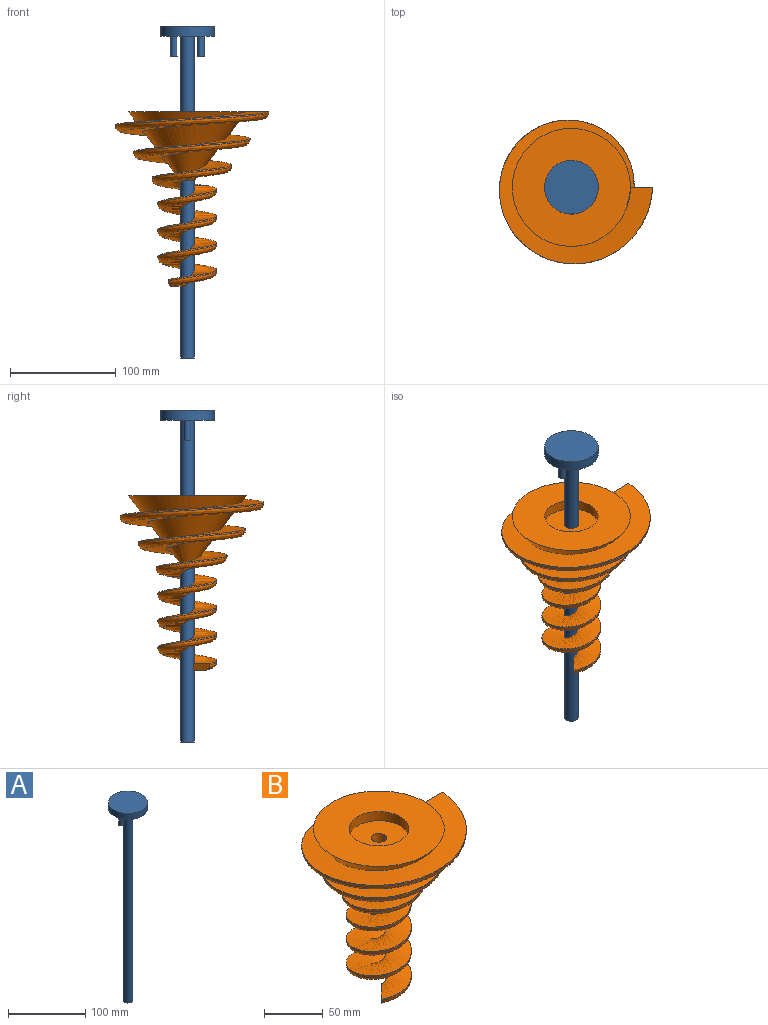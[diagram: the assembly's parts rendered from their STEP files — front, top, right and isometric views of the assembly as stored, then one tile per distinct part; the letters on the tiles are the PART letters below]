
ASSEMBLY  parts=2 mates=1
PART A: 9 faces, bbox 50.8x50.8x314.3 mm
  f0: cylinder r=25.4mm len=50.8mm, axis (0,0,1), area 1520.1mm2, adj f1,f2
  f1: plane 50.8x50.8mm, normal (0,0,-1), area 1836.8mm2, adj f0,f3,f5,f7
  f2: plane 50.8x50.8mm, normal (0,0,1), area 2026.8mm2, adj f0
  f3: cylinder r=6.35mm len=304.8mm, axis (0,0,1), area 12161mm2, adj f1,f4
  f4: plane 12.7x12.7mm, normal (0,0,-1), area 126.7mm2, adj f3
  f5: cylinder r=3.17mm len=19.05mm, axis (0,0,1), area 380mm2, adj f1,f6
  f6: plane 6.35x6.35mm, normal (0,0,-1), area 31.7mm2, adj f5
  f7: cylinder r=3.17mm len=19.05mm, axis (0,0,1), area 380mm2, adj f1,f8
  f8: plane 6.35x6.35mm, normal (0,0,-1), area 31.7mm2, adj f7
PART B: 36 faces, bbox 145.4x137.7x165.3 mm
  f0: bspline ~89.48x85.12mm, area 645.8mm2, adj f1,f5,f9,f21,f22,f23
  f1: cone r=55.88mm half-angle=37.4deg, axis (0,0,1), area 12469.1mm2, adj f0,f2,f4,f5,f6,f9,f17,f18
  f2: plane 25.8x6.35mm, normal (0,1,0), area 142.9mm2, adj f1,f3,f4,f5,f31
  f3: bspline ~145.32x137.61mm, area 1159.1mm2, adj f2,f4,f29,f31
  f4: bspline ~145.32x137.61mm, area 16660.8mm2, adj f1,f2,f3,f9,f17,f18,f20,f30
  f5: bspline ~145.32x137.61mm, area 13749.4mm2, adj f0,f1,f2,f9,f24,f25,f26,f28
  f6: plane 111.76x111.76mm, normal (0,0,1), area 7783mm2, adj f1,f7
  f7: cylinder r=25.4mm len=50.8mm, axis (0,0,1), area 1520.1mm2, adj f6,f8
  f8: plane 50.8x50.8mm, normal (0,0,1), area 1895mm2, adj f7,f9
  f9: cylinder r=6.48mm len=71.01mm, axis (0,0,1), area 2363.8mm2, adj f0,f1,f4,f5,f8,f10,f14,f15
  f10: cylinder r=6.48mm len=31.75mm, axis (0,0,1), area 258.4mm2, adj f9,f11,f28,f30
  f11: cylinder r=6.48mm len=31.75mm, axis (0,0,1), area 258.4mm2, adj f10,f12,f28,f30
  f12: cylinder r=6.48mm len=31.75mm, axis (0,0,1), area 258.4mm2, adj f11,f13,f28,f30
  f13: cylinder r=6.48mm len=14.71mm, axis (0,0,1), area 85.1mm2, adj f12,f27,f28,f30
  f14: bspline ~4.57x2.65mm, area 0mm2, adj f9,f15,f16
  f15: bspline ~7.2x7.06mm, area 3.7mm2, adj f9,f14,f16
  f16: plane 3.92x2.43mm, normal (0.39,0.74,-0.55), area 0.5mm2, adj f9,f14,f15
  f17: bspline ~2.12x1.49mm, area 0.6mm2, adj f1,f4,f19,f20
  f18: bspline ~4.45x2.8mm, area 1.8mm2, adj f1,f4,f19,f20
  f19: bspline ~2.48x1.6mm, area 1.4mm2, adj f1,f17,f18,f20
  f20: plane 0.69x0.46mm, normal (0.39,0.74,-0.55), area 0.2mm2, adj f4,f17,f18,f19
  f21: bspline ~76.8x75.65mm, area 538.5mm2, adj f0,f1,f22
  f22: bspline ~84.06x75.39mm, area 149.2mm2, adj f0,f1,f21,f23
  f23: bspline ~76.08x74.82mm, area 439.7mm2, adj f0,f1,f22
  f24: bspline ~2.34x1.4mm, area 0.7mm2, adj f5,f25,f26
  f25: plane 2.3x1.23mm, normal (0.39,0.74,-0.55), area 0.2mm2, adj f5,f24,f26
  f26: bspline ~7.7x4.39mm, area 0.1mm2, adj f5,f24,f25
  f27: plane 15.4x15.17mm, normal (-0.71,0.7,0), area 131.8mm2, adj f13,f28,f29,f30,f32
  f28: bspline ~89.87x58.46mm, area 5515.2mm2, adj f5,f9,f10,f11,f12,f13,f27,f31
  f29: cylinder r=27.9mm len=90.15mm, axis (0,0,-1), area 805.1mm2, adj f3,f27,f30,f31,f32
  f30: bspline ~88.9x55.76mm, area 8359.3mm2, adj f4,f9,f10,f11,f12,f13,f27,f29
  f31: bspline ~145.02x136.29mm, area 7234.5mm2, adj f2,f3,f5,f28,f29,f32
  f32: bspline ~94.32x55.85mm, area 4608.4mm2, adj f27,f28,f29,f31
  f33: bspline ~26.57x13.94mm, area 0mm2, adj f34,f35
  f34: cone r=55.88mm half-angle=37.4deg, axis (0,0,1), area 0mm2, adj f33,f35
  f35: bspline ~19.75x14.63mm, area 0mm2, adj f33,f34
PLACE A t=(-13.69,-16.61,303.07)mm
PLACE B t=(-13.69,-16.61,151.99)mm
MATE cylindrical A.f3 <-> B.f9  axis (0,0,1) through (-13.69,-16.61,141.15)mm
